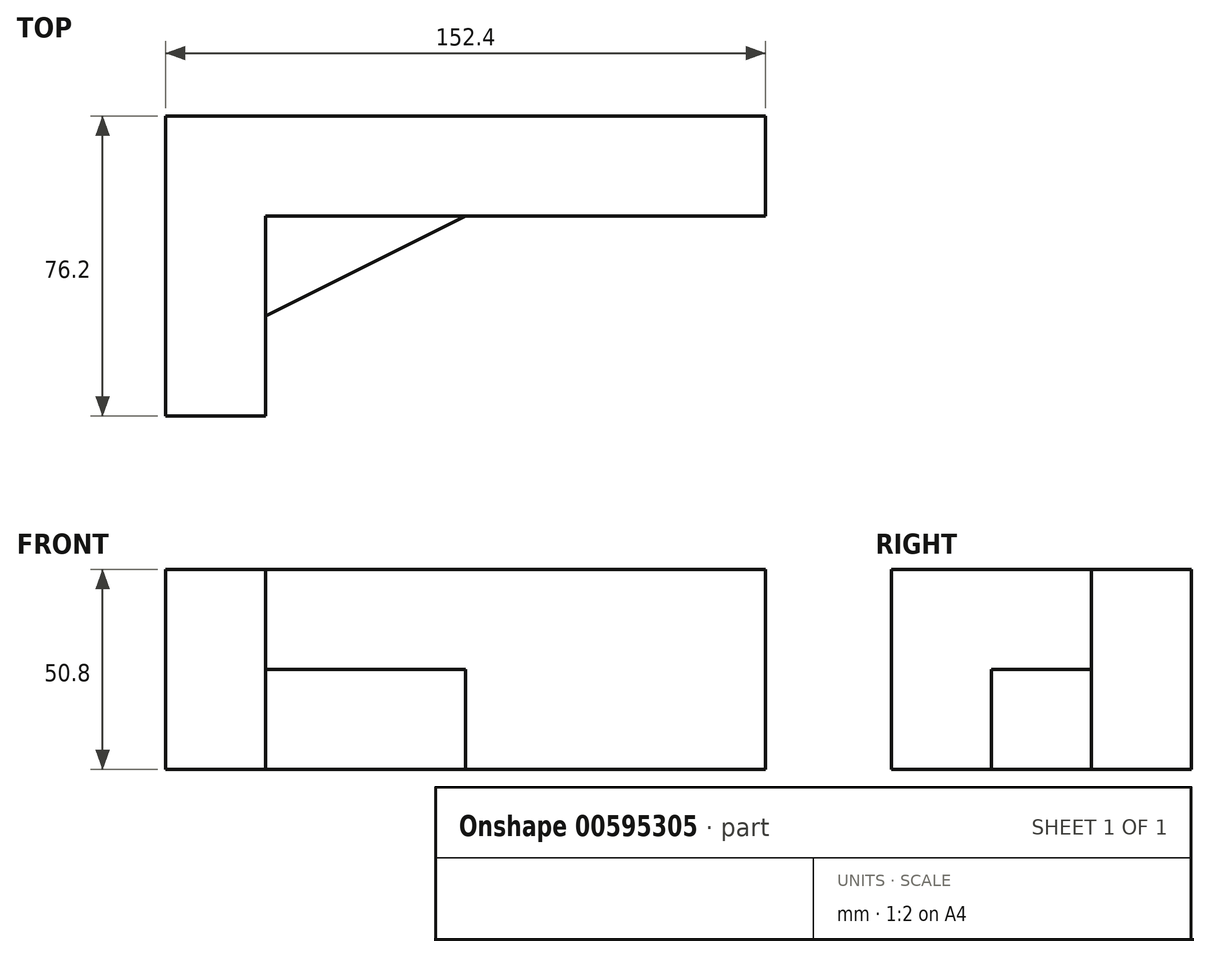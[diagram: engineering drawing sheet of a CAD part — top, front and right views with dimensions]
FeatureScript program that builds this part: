
annotation { "Feature Type Name" : "Feature", "Feature Type Description" : "" }
export const myFeature = defineFeature(function(context is Context, id is Id, definition is map)
    precondition{}
    {
        {
            var Q0;
            Q0=qCreatedBy(makeId("Top.planeOp"),FACE);
            var sketch = newSketch(context, id + "F0", { "sketchPlane" : qUnion([Q0])});
            skLineSegment(sketch, "E0.bottom", {"start": v(0, 0) * mm, "end": v(25.4, 0) * mm});
            skLineSegment(sketch, "E0.top", {"start": v(0, 76.2) * mm, "end": v(152.4, 76.2) * mm});
            skLineSegment(sketch, "E0.left", {"start": v(0, 0) * mm, "end": v(0, 76.2) * mm});
            skLineSegment(sketch, "E1", {"start": v(25.4, 0) * mm, "end": v(25.4, 50.8) * mm});
            skLineSegment(sketch, "E2", {"start": v(25.4, 50.8) * mm, "end": v(152.4, 50.8) * mm});
            skLineSegment(sketch, "E3", {"start": v(152.4, 50.8) * mm, "end": v(152.4, 76.2) * mm});
            skSolve(sketch);
        }
        {
            var Q0;
            Q0 = qSketchRegion(id + "F0", true);
            extrude(context, id + "F1", {"entities" : qUnion([Q0]), "depth" : 50.8 * mm, "offsetDistance" : 25.4 * mm});
        }
        {
            var Q0;
            Q0=makeQuery(id+"F1.opExtrude","CAP_FACE",FACE,{"disambiguationData":[OSD([sQuery(id+"F0.wireOp",EDGE,"E0.bottom"),sQuery(id+"F0.wireOp",EDGE,"E0.top"),sQuery(id+"F0.wireOp",EDGE,"E0.left"),sQuery(id+"F0.wireOp",EDGE,"E1"),sQuery(id+"F0.wireOp",EDGE,"E2"),sQuery(id+"F0.wireOp",EDGE,"E3")])],"isStart":false});
            cPlane(context, id + "F2", {"entities" : qUnion([Q0]), "cplaneType" : CPlaneType.OFFSET, "offset" : 25.4 * mm, "oppositeDirection" : true, "width" : 152.4 * mm, "height" : 152.4 * mm});
        }
        {
            var Q0;
            Q0=qCreatedBy(id+"F2.planeOp",FACE);
            var sketch = newSketch(context, id + "F3", { "sketchPlane" : qUnion([Q0])});
            skLineSegment(sketch, "E4", {"start": v(25.4, 25.4) * mm, "end": v(76.2, 50.8) * mm});
            skLineSegment(sketch, "E5", {"start": v(25.4, 50.8) * mm, "end": v(76.2, 50.8) * mm});
            skPoint(sketch, "E6.start.orphan", {"position": v(0, 50.8) * mm});
            skLineSegment(sketch, "E7", {"start": v(152.4, 50.8) * mm, "end": v(152.4, 50.8) * mm});
            skLineSegment(sketch, "E8", {"start": v(25.4, 25.4) * mm, "end": v(25.4, 50.8) * mm});
            skPoint(sketch, "E9.start.orphan", {"position": v(25.4, 0) * mm});
            skSolve(sketch);
        }
        {
            var Q0;
            Q0 = qSketchRegion(id + "F3", true);
            extrude(context, id + "F4", {"entities" : qUnion([Q0]), "operationType" : NewBodyOperationType.ADD, "oppositeDirection" : true, "depth" : 25.4 * mm, "offsetDistance" : 25.4 * mm});
        }
    });
